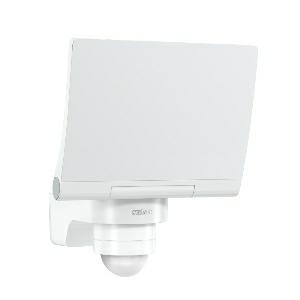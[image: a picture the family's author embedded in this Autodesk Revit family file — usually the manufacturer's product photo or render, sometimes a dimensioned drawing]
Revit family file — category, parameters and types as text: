
# Revit family: xled_pro_240_068073
name_source: partatom
category: Leuchten
revit_build: Autodesk Revit 2016 (Build: 20190508_0715(x64)
units: mm (PartAtom-declared; Revit-internal decimal feet)

## family parameters
Basisbauteil = Fläche
Beim Laden mit Abzugskörper schneiden = Nein
Bemaßung runder Anschluss = Durchmesser verwenden
Gemeinsam genutzt = Nein
Lichtquelle = Nein
Raumberechnungspunkt = Nein
Teiletyp = Normal

## types (1)
- XLED PRO 240 (1 x , 2120 lm, 3000 K)
    Beschreibung = Dimensions (L x W x H): 161 x 180 x 221 mm; Mains power supply: 230 – 240 V / 50 – 60 Hz; Mounting height max.: 6,00 m; Sensor Technology: passive infrared; Output: 20 W; Interconnection: Yes; Switching output 1, resistive: 1000 W; Luminous flux: 2120 lm; Colour temperature: 3000 K; Colour variation LED: SDCM3; Colour Rendering Index CRI: 80-89; With lamp: Yes, STEINEL LED system; Lamp: LED cannot be replaced; LED life expectancy (max. °C): 60000 h; Drop in luminous flux in accordance with LM80: L70B10; LED cooling system: HCMC (High Conductive Magnesium Composite); With motion detector: Yes; Detection angle: 240 °; Angle of aperture: 180 °; Sneak-by guard: Yes; Capability of masking out individual segments: Yes; Reach, radial: r = 3 m (19 m²); Reach, tangential: r = 12 m (302 m²); Photo-cell controller: Yes; Twilight setting: 2 – 1000 lx; Time setting: 10 sec – 15 min; Basic light level function: No; Soft light start: No; Continuous light: selectable; Impact resistance: IK03; IP-rating: IP44; Protection class: II; Ambient temperature: -20 – 40 °C; Housing material: HCMC; Cover material: Plastic, opal; Manufacturer's Warranty: 5 years; Includes corner wall mount: Yes; PU1, net weight: 0,64 kg; Version: warm white white; PU1, EAN: 4007841068073
    Color Rendering = 80-89
    Color Temperature = 3000 K
    Frequency = 60 Hz, 50 Hz
    Height = 221 mm
    Hersteller = Steinel
    Lamp Light Flux = 2120 lm
    Lamp count = 1
    Lampe = 1 x
    Length = 161 mm
    Luminous efficacy = 0 lm/W
    ModVariant = Nein
    Modell = 068073
    Mounting Type = Surface mounted
    Number of Poles = 1
    OnlyDefault = Ja
    Power Factor = 1
    Product Name = XLED PRO 240
    Product group = Sensor-switched indoor light
    ProductGroupID = 30
    Protection Class = Protection class II
    Protection Degree = IP 34
    RlxData = <blob elided: 64009 chars, md5=7579b589>
    Scheinlast = 20 VA
    Socket = socket
    Standby Power = 0 W
    System Light Flux = 0 lm
    System Power = 20 W
    Typenbild = produkt1_068073.jpg
    Typenkommentare = Product without accessories
    URL = http://relux.com
    VarID = ---
    Voltage = 0 V
    Vorgabe-Ansicht = 1800 mm
    Weight = 0.00 kg
    Width = 180 mm  [stored 0.590551 ft]

note: [stored X ft] marks values corroborated as IEEE doubles in the binary element streams (Revit-internal decimal feet)

## geometry (parser evidence)
native form markers: Blend x4, Sweep x13
no freeform markers — native parametric forms only
